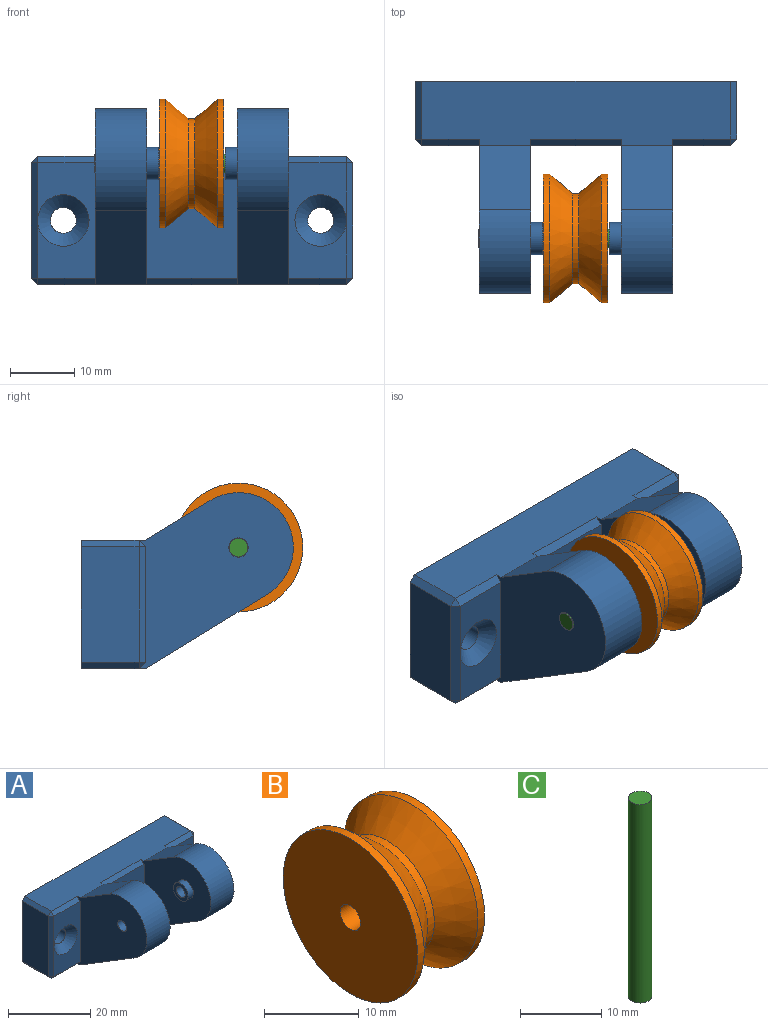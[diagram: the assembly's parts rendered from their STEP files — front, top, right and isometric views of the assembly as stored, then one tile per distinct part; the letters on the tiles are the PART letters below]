
ASSEMBLY  parts=3 mates=2
PART A: 44 faces, bbox 50x33x27.4 mm
  f0: plane 18x14mm, normal (0,-1,0), area 252mm2, adj f12,f18,f36,f37
  f1: plane 18x9mm, normal (0,-1,0), area 111.7mm2, adj f13,f30,f32,f33,f43
  f2: plane 48x10mm, normal (0,0,1), area 448mm2, adj f7,f8,f12,f13,f14,f18,f19,f25
  f3: plane 18x9mm, normal (-1,0,0), area 162mm2, adj f7,f23,f26,f28
  f4: plane 48x10mm, normal (0,0,-1), area 448mm2, adj f7,f10,f12,f13,f16,f18,f19,f22
  f5: plane 18x9mm, normal (1,0,0), area 162mm2, adj f7,f29,f32,f35
  f6: plane 18x9mm, normal (0,-1,0), area 111.7mm2, adj f19,f22,f25,f26,f42
  f7: plane 50x20mm, normal (0,1,0), area 972.9mm2, adj f2,f3,f4,f5,f20,f21,f23,f28
  f8: plane 10x8mm, normal (0,0.52,0.85), area 93.8mm2, adj f2,f9,f12,f13
  f9: cylinder r=8.53mm len=15.8mm, axis (1,0,0), area 214.3mm2, adj f8,f10,f12,f13
  f10: plane 18.91x11.58mm, normal (0,-0.52,-0.85), area 177.4mm2, adj f4,f9,f12,f13
  f11: cylinder r=1.5mm len=9.8mm, axis (1,0,0), area 92.4mm2, adj f13,f41
  f12: plane 27.38x23.98mm, normal (-1,0,0), area 384.7mm2, adj f0,f2,f4,f8,f9,f10,f36,f37
  f13: plane 27.38x23.98mm, normal (1,0,0), area 397.2mm2, adj f1,f2,f4,f8,f9,f10,f11,f30
  f14: plane 10x8mm, normal (0,0.52,0.85), area 93.8mm2, adj f2,f15,f18,f19
  f15: cylinder r=8.53mm len=15.8mm, axis (-1,0,0), area 214.3mm2, adj f14,f16,f18,f19
  f16: plane 18.91x11.58mm, normal (0,-0.52,-0.85), area 177.4mm2, adj f4,f15,f18,f19
  f17: cylinder r=1.5mm len=9.8mm, axis (-1,0,0), area 92.4mm2, adj f19,f39
  f18: plane 27.38x23.98mm, normal (1,0,0), area 384.7mm2, adj f0,f2,f4,f14,f15,f16,f36,f37
  f19: plane 27.38x23.98mm, normal (-1,0,0), area 397.2mm2, adj f2,f4,f6,f14,f15,f16,f17,f22
  f20: cylinder r=2mm len=8mm, axis (0,1,0), area 100.5mm2, adj f7,f42
  f21: cylinder r=2mm len=8mm, axis (0,1,0), area 100.5mm2, adj f7,f43
  f22: plane 9x1mm, normal (0,-0.71,-0.71), area 12.7mm2, adj f4,f6,f19,f24
  f23: plane 9x1mm, normal (-0.71,0,-0.71), area 12.7mm2, adj f3,f4,f7,f24
  f24: plane 1x1mm, normal (-0.58,-0.58,-0.58), area 0.9mm2, adj f22,f23,f26
  f25: plane 9x1mm, normal (0,-0.71,0.71), area 12.7mm2, adj f2,f6,f19,f27
  f26: plane 18x1mm, normal (-0.71,-0.71,0), area 25.5mm2, adj f3,f6,f24,f27
  f27: plane 1x1mm, normal (-0.58,-0.58,0.58), area 0.9mm2, adj f25,f26,f28
  f28: plane 9x1mm, normal (-0.71,0,0.71), area 12.7mm2, adj f2,f3,f7,f27
  f29: plane 9x1mm, normal (0.71,0,-0.71), area 12.7mm2, adj f4,f5,f7,f31
  f30: plane 9x1mm, normal (0,-0.71,-0.71), area 12.7mm2, adj f1,f4,f13,f31
  f31: plane 1x1mm, normal (0.58,-0.58,-0.58), area 0.9mm2, adj f29,f30,f32
  f32: plane 18x1mm, normal (0.71,-0.71,0), area 25.5mm2, adj f1,f5,f31,f34
  f33: plane 9x1mm, normal (0,-0.71,0.71), area 12.7mm2, adj f1,f2,f13,f34
  f34: plane 1x1mm, normal (0.58,-0.58,0.58), area 0.9mm2, adj f32,f33,f35
  f35: plane 9x1mm, normal (0.71,0,0.71), area 12.7mm2, adj f2,f5,f7,f34
  f36: plane 14x1mm, normal (0,-0.71,0.71), area 19.8mm2, adj f0,f2,f12,f18
  f37: plane 14x1mm, normal (0,-0.71,-0.71), area 19.8mm2, adj f0,f4,f12,f18
  f38: cylinder r=2.5mm len=5mm, axis (-1,0,0), area 28.3mm2, adj f18,f39
  f39: plane 5x5mm, normal (1,0,0), area 12.6mm2, adj f17,f38
  f40: cylinder r=2.5mm len=5mm, axis (1,0,0), area 28.3mm2, adj f12,f41
  f41: plane 5x5mm, normal (-1,0,0), area 12.6mm2, adj f11,f40
  f42: cone r=2mm half-angle=45deg, axis (0,-1,0), area 53.3mm2, adj f6,f20
  f43: cone r=2mm half-angle=45deg, axis (0,-1,0), area 53.3mm2, adj f1,f21
PART B: 8 faces, bbox 10x20x20 mm
  f0: plane 20x20mm, normal (-1,0,0), area 307.1mm2, adj f1,f7
  f1: cylinder r=10mm len=20mm, axis (-1,0,0), area 62.8mm2, adj f0,f2
  f2: cone r=10mm half-angle=40.6deg, axis (-1,0,0), area 246.2mm2, adj f1,f3
  f3: cylinder r=7mm len=14mm, axis (-1,0,0), area 44mm2, adj f2,f4
  f4: cone r=7mm half-angle=40.6deg, axis (1,0,0), area 246.2mm2, adj f3,f5
  f5: cylinder r=10mm len=20mm, axis (-1,0,0), area 62.8mm2, adj f4,f6
  f6: plane 20x20mm, normal (1,0,0), area 307.1mm2, adj f5,f7
  f7: cylinder r=1.5mm len=10mm, axis (1,0,0), area 94.2mm2, adj f0,f6
PART C: 3 faces, bbox 2.9x2.9x30 mm
  f0: cylinder r=1.45mm len=30mm, axis (0,0,-1), area 273.3mm2, adj f1,f2
  f1: plane 2.9x2.9mm, normal (0,0,1), area 6.6mm2, adj f0
  f2: plane 2.9x2.9mm, normal (0,0,-1), area 6.6mm2, adj f0
PLACE A t=(-1.03,18.53,26.47)mm
PLACE B rot(axis=(0.64,0.77,0),0deg) t=(-1.09,-5.92,35.32)mm
PLACE C rot(axis=(0,-1,0),90deg) t=(13.83,-5.92,35.32)mm
MATE slider B.f2 <-> C.f0  axis (-1,0,0) through (-6.09,-5.92,35.32)mm
MATE cylindrical C.f0 <-> A.f9  axis (1,0,0) through (13.83,-5.92,35.32)mm
